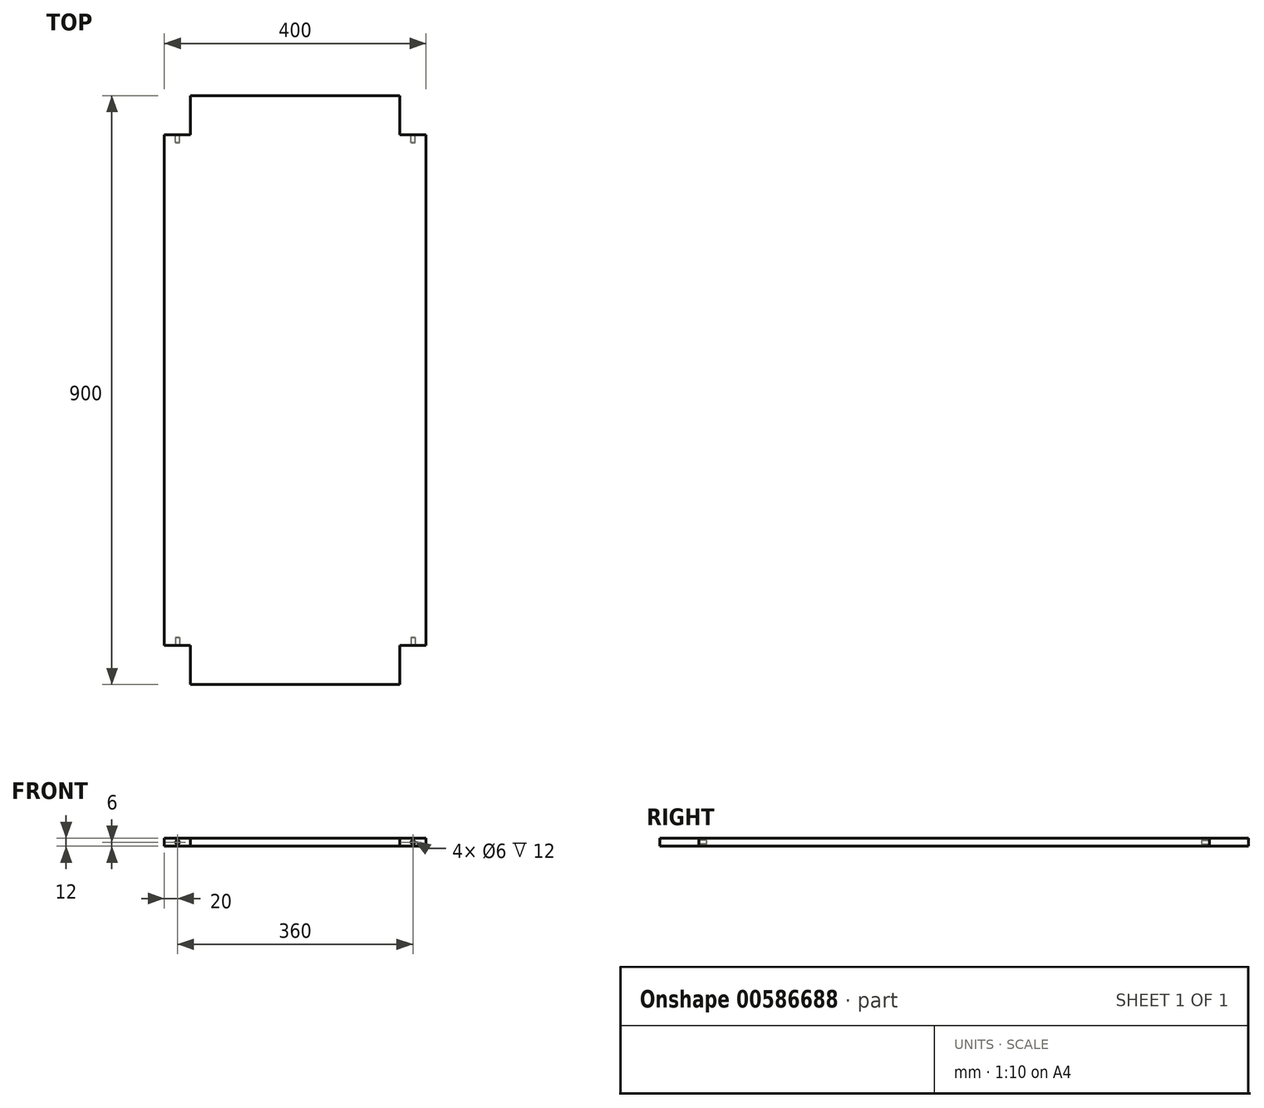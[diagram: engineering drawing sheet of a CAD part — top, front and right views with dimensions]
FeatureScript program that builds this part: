
annotation { "Feature Type Name" : "Feature", "Feature Type Description" : "" }
export const myFeature = defineFeature(function(context is Context, id is Id, definition is map)
    precondition{}
    {
        {
            var Q0;
            Q0=qCreatedBy(makeId("Front.planeOp"),FACE);
            var sketch = newSketch(context, id + "F0", { "sketchPlane" : qUnion([Q0])});
            skLineSegment(sketch, "E0.bottom", {"start": v(0, 0) * mm, "end": v(400, 0) * mm});
            skLineSegment(sketch, "E0.top", {"start": v(0, 12) * mm, "end": v(400, 12) * mm});
            skLineSegment(sketch, "E0.left", {"start": v(0, 0) * mm, "end": v(0, 12) * mm});
            skLineSegment(sketch, "E0.right", {"start": v(400, 0) * mm, "end": v(400, 12) * mm});
            skSolve(sketch);
        }
        {
            var Q0;
            Q0 = qSketchRegion(id + "F0", true);
            extrude(context, id + "F1", {"entities" : qUnion([Q0]), "depth" : 900 * mm, "offsetDistance" : 25 * mm, "symmetric" : true});
        }
        {
            var Q0;
            Q0=makeQuery(id+"F1.opExtrude","SWEPT_FACE",FACE,{"disambiguationData":[OSD([sQuery(id+"F0.wireOp",EDGE,"E0.top")])]});
            var sketch = newSketch(context, id + "F2", { "sketchPlane" : qUnion([Q0])});
            skLineSegment(sketch, "E1.bottom", {"start": v(0, 450) * mm, "end": v(40, 450) * mm});
            skLineSegment(sketch, "E1.top", {"start": v(0, 390) * mm, "end": v(40, 390) * mm});
            skLineSegment(sketch, "E1.left", {"start": v(0, 450) * mm, "end": v(0, 390) * mm});
            skLineSegment(sketch, "E1.right", {"start": v(40, 450) * mm, "end": v(40, 390) * mm});
            skSolve(sketch);
        }
        {
            var Q0;
            Q0 = qSketchRegion(id + "F2", true);
            extrude(context, id + "F3", {"entities" : qUnion([Q0]), "operationType" : NewBodyOperationType.REMOVE, "oppositeDirection" : true, "depth" : 12 * mm, "offsetDistance" : 25 * mm});
        }
        {
            var Q0;
            Q0=makeQuery(id+"F1.opExtrude","SWEPT_FACE",FACE,{"disambiguationData":[OSD([sQuery(id+"F0.wireOp",EDGE,"E0.top")])]});
            var sketch = newSketch(context, id + "F4", { "sketchPlane" : qUnion([Q0])});
            skLineSegment(sketch, "E2.bottom", {"start": v(400, 450) * mm, "end": v(360, 450) * mm});
            skLineSegment(sketch, "E2.top", {"start": v(400, 390) * mm, "end": v(360, 390) * mm});
            skLineSegment(sketch, "E2.left", {"start": v(400, 450) * mm, "end": v(400, 390) * mm});
            skLineSegment(sketch, "E2.right", {"start": v(360, 450) * mm, "end": v(360, 390) * mm});
            skSolve(sketch);
        }
        {
            var Q0;
            Q0 = qSketchRegion(id + "F4", true);
            extrude(context, id + "F5", {"entities" : qUnion([Q0]), "operationType" : NewBodyOperationType.REMOVE, "oppositeDirection" : true, "depth" : 15 * mm, "offsetDistance" : 25 * mm});
        }
        {
            var Q0;
            Q0=makeQuery(id+"F1.opExtrude","SWEPT_FACE",FACE,{"disambiguationData":[OSD([sQuery(id+"F0.wireOp",EDGE,"E0.top")])]});
            var sketch = newSketch(context, id + "F6", { "sketchPlane" : qUnion([Q0])});
            skLineSegment(sketch, "E3.bottom", {"start": v(400, -450) * mm, "end": v(360, -450) * mm});
            skLineSegment(sketch, "E3.top", {"start": v(400, -390) * mm, "end": v(360, -390) * mm});
            skLineSegment(sketch, "E3.left", {"start": v(400, -450) * mm, "end": v(400, -390) * mm});
            skLineSegment(sketch, "E3.right", {"start": v(360, -450) * mm, "end": v(360, -390) * mm});
            skSolve(sketch);
        }
        {
            var Q0;
            Q0 = qSketchRegion(id + "F6", true);
            extrude(context, id + "F7", {"entities" : qUnion([Q0]), "operationType" : NewBodyOperationType.REMOVE, "oppositeDirection" : true, "depth" : 15 * mm, "offsetDistance" : 25 * mm});
        }
        {
            var Q0;
            Q0=makeQuery(id+"F1.opExtrude","SWEPT_FACE",FACE,{"disambiguationData":[OSD([sQuery(id+"F0.wireOp",EDGE,"E0.top")])]});
            var sketch = newSketch(context, id + "F8", { "sketchPlane" : qUnion([Q0])});
            skLineSegment(sketch, "E4.bottom", {"start": v(0, -450) * mm, "end": v(40, -450) * mm});
            skLineSegment(sketch, "E4.top", {"start": v(0, -390) * mm, "end": v(40, -390) * mm});
            skLineSegment(sketch, "E4.left", {"start": v(0, -450) * mm, "end": v(0, -390) * mm});
            skLineSegment(sketch, "E4.right", {"start": v(40, -450) * mm, "end": v(40, -390) * mm});
            skSolve(sketch);
        }
        {
            var Q0;
            Q0 = qSketchRegion(id + "F8", true);
            extrude(context, id + "F9", {"entities" : qUnion([Q0]), "operationType" : NewBodyOperationType.REMOVE, "oppositeDirection" : true, "depth" : 15 * mm, "offsetDistance" : 25 * mm});
        }
        {
            var Q0;
            Q0=makeQuery(id+"F9.boolean.opBoolean","COPY",FACE,{"derivedFrom":makeQuery(id+"F9.opExtrude","SWEPT_FACE",FACE,{"disambiguationData":[OSD([sQuery(id+"F8.wireOp",EDGE,"E4.top")])]})});
            var sketch = newSketch(context, id + "F10", { "sketchPlane" : qUnion([Q0])});
            skCircle(sketch, "E5", {"center": v(20, 6) * mm, "radius": 3 * mm});
            skSolve(sketch);
        }
        {
            var Q0;
            Q0 = qSketchRegion(id + "F10", true);
            extrude(context, id + "F11", {"entities" : qUnion([Q0]), "operationType" : NewBodyOperationType.REMOVE, "oppositeDirection" : true, "depth" : 12 * mm, "offsetDistance" : 25 * mm});
        }
        {
            var Q0;
            Q0=makeQuery(id+"F7.boolean.opBoolean","COPY",FACE,{"derivedFrom":makeQuery(id+"F7.opExtrude","SWEPT_FACE",FACE,{"disambiguationData":[OSD([sQuery(id+"F6.wireOp",EDGE,"E3.top")])]})});
            var sketch = newSketch(context, id + "F12", { "sketchPlane" : qUnion([Q0])});
            skCircle(sketch, "E6", {"center": v(380, 6) * mm, "radius": 3 * mm});
            skSolve(sketch);
        }
        {
            var Q0;
            Q0 = qSketchRegion(id + "F12", true);
            extrude(context, id + "F13", {"entities" : qUnion([Q0]), "operationType" : NewBodyOperationType.REMOVE, "oppositeDirection" : true, "depth" : 12 * mm, "offsetDistance" : 25 * mm});
        }
        {
            var Q0;
            Q0=makeQuery(id+"F5.boolean.opBoolean","COPY",FACE,{"derivedFrom":makeQuery(id+"F5.opExtrude","SWEPT_FACE",FACE,{"disambiguationData":[OSD([sQuery(id+"F4.wireOp",EDGE,"E2.top")])]})});
            var sketch = newSketch(context, id + "F14", { "sketchPlane" : qUnion([Q0])});
            skCircle(sketch, "E7.0", {"center": v(-380, 6) * mm, "radius": 3 * mm});
            skSolve(sketch);
        }
        {
            var Q0;
            Q0 = qSketchRegion(id + "F14", true);
            extrude(context, id + "F15", {"entities" : qUnion([Q0]), "operationType" : NewBodyOperationType.REMOVE, "oppositeDirection" : true, "depth" : 12 * mm, "offsetDistance" : 25 * mm});
        }
        {
            var Q0;
            Q0=makeQuery(id+"F3.boolean.opBoolean","COPY",FACE,{"derivedFrom":makeQuery(id+"F3.opExtrude","SWEPT_FACE",FACE,{"disambiguationData":[OSD([sQuery(id+"F2.wireOp",EDGE,"E1.top")])]})});
            var sketch = newSketch(context, id + "F16", { "sketchPlane" : qUnion([Q0])});
            skCircle(sketch, "E8.0", {"center": v(-20, 6) * mm, "radius": 3 * mm});
            skSolve(sketch);
        }
        {
            var Q0;
            Q0 = qSketchRegion(id + "F16", true);
            extrude(context, id + "F17", {"entities" : qUnion([Q0]), "operationType" : NewBodyOperationType.REMOVE, "oppositeDirection" : true, "depth" : 12 * mm, "offsetDistance" : 25 * mm});
        }
    });
